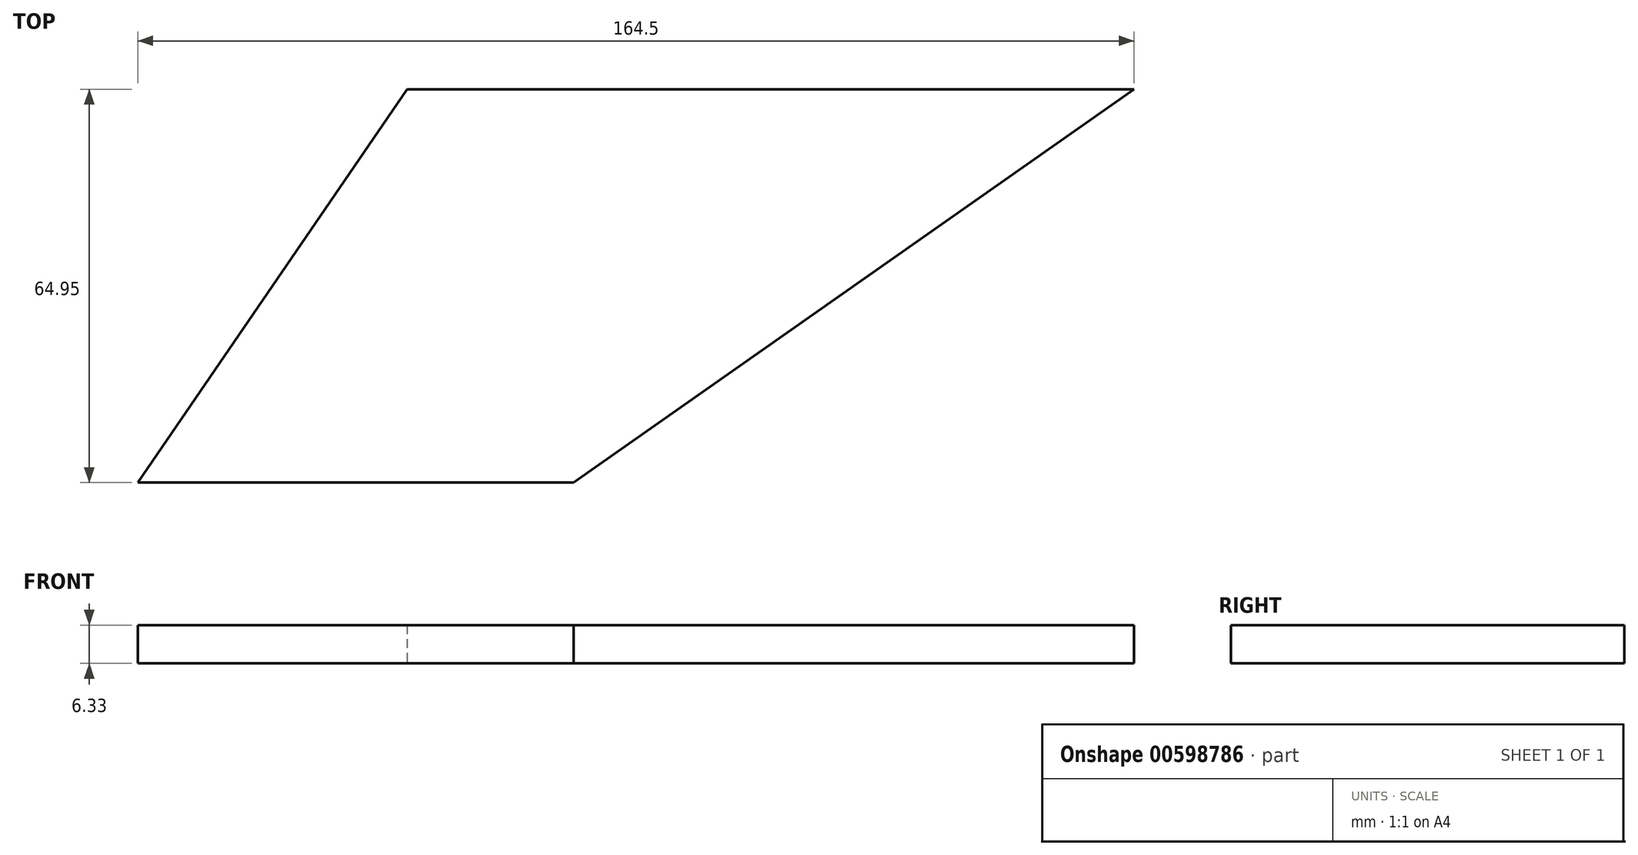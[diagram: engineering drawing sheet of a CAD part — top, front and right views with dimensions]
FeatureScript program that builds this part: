
annotation { "Feature Type Name" : "Feature", "Feature Type Description" : "" }
export const myFeature = defineFeature(function(context is Context, id is Id, definition is map)
    precondition{}
    {
        {
            var Q0;
            Q0=qCreatedBy(makeId("Top.planeOp"),FACE);
            var sketch = newSketch(context, id + "F0", { "sketchPlane" : qUnion([Q0])});
            skLineSegment(sketch, "E0", {"start": v(-17.3, 64.95) * mm, "end": v(102.7, 64.95) * mm});
            skLineSegment(sketch, "E1", {"start": v(-54.8, 0) * mm, "end": v(10.2, 0) * mm});
            skLineSegment(sketch, "E2", {"start": v(10.2, 0) * mm, "end": v(102.7, 64.95) * mm});
            skLineSegment(sketch, "E3", {"start": v(-54.8, 0) * mm, "end": v(-61.8, 0) * mm});
            skLineSegment(sketch, "E4", {"start": v(-61.8, 0) * mm, "end": v(-17.3, 64.95) * mm});
            skSolve(sketch);
        }
        {
            var Q0;
            Q0=makeQuery(id+"F0.imprint","IMPRINT",FACE,{"disambiguationData":[TD([[makeQuery(id+"F0.imprint","IMPRINT",EDGE,{"derivedFrom":sQuery(id+"F0.wireOp",EDGE,"E0")}),-1.0]])]});
            extrude(context, id + "F1", {"entities" : qUnion([Q0]), "depth" : 6.33 * mm, "offsetDistance" : 25 * mm});
        }
    });
